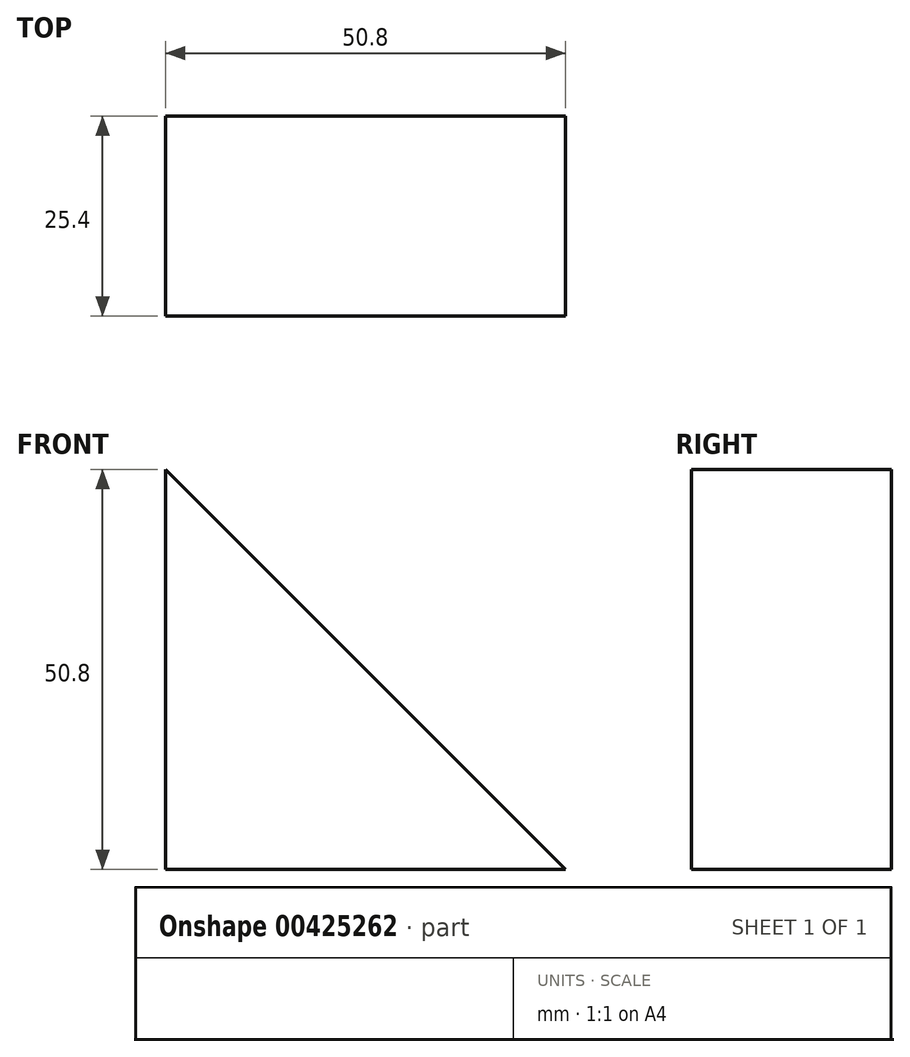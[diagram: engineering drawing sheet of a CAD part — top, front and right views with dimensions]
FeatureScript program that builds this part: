
annotation { "Feature Type Name" : "Feature", "Feature Type Description" : "" }
export const myFeature = defineFeature(function(context is Context, id is Id, definition is map)
    precondition{}
    {
        {
            var Q0;
            Q0=qCreatedBy(makeId("Front.planeOp"),FACE);
            var sketch = newSketch(context, id + "F0", { "sketchPlane" : qUnion([Q0])});
            skLineSegment(sketch, "E0", {"start": v(-37.62, 78.49) * mm, "end": v(-37.62, 27.69) * mm});
            skLineSegment(sketch, "E1", {"start": v(-37.62, 27.69) * mm, "end": v(13.18, 27.69) * mm});
            skLineSegment(sketch, "E2", {"start": v(-37.62, 78.49) * mm, "end": v(13.18, 27.69) * mm});
            skSolve(sketch);
        }
        {
            var Q0;
            Q0=makeQuery(id+"F0.imprint","IMPRINT",FACE,{"disambiguationData":[TD([[makeQuery(id+"F0.imprint","IMPRINT",EDGE,{"derivedFrom":sQuery(id+"F0.wireOp",EDGE,"E0")}),1.0]])]});
            extrude(context, id + "F1", {"entities" : qUnion([Q0]), "depth" : 25.4 * mm});
        }
    });
